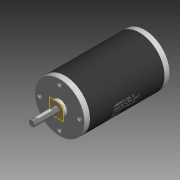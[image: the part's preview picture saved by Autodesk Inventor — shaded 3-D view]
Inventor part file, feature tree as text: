
AUTODESK INVENTOR PART (.ipt)
format: ipt  version: 2018 (Build 220112000, 112)  size: 7,095,296 bytes
history: native  units: mm (DEFAULTED — no unit token found)
features: sketch x10, extrude x7, chamfer x4, plane x3, hole x2, pattern_circular x2, fillet x2, emboss x1, split x1
ambient origin geometry x8: Origin, YZ Plane, XZ Plane, XY Plane, X Axis, Y Axis, Z Axis, Center Point
bodies: Solid1 (feature_tree), Solid2 (feature_tree), Solid3 (feature_tree)
feature tree (32):
  extrude  "Extrusion1"  Depth=7.0mm TaperAngle=0.0deg
  extrude  "Extrusion2"  Depth=3.9878mm TaperAngle=0.0deg
  chamfer  "Chamfer1"  Distance=1.0mm
  hole  "Hole2"  [1 undecoded]
  pattern_circular  "Circular Pattern2"  Count=4 Angle=90.0deg
  chamfer  "Chamfer3"  Distance=31.623mm
  extrude  "Extrusion3"  Depth=12.7mm
  fillet  "Fillet1"  Radius=64.4144mm
  extrude  "Extrusion5"  Depth=64.008mm
  extrude  "Extrusion6"  Depth=7.0mm
  extrude  "Extrusion7"  Depth=0.508mm
  hole  "Hole3"  [1 undecoded]
  chamfer  "Chamfer2"  Distance=20.0mm Angle=360.0deg
  pattern_circular  "Circular Pattern3"  [2 undecoded]
  fillet  "Fillet2"  [1 undecoded]
  chamfer  "Chamfer4"  Distance=1.99898mm
  plane  "Work Plane1"
  extrude  "Extrusion8"  Depth=1.99898mm
  plane  "Work Plane2"
  emboss  "Emboss1"
  plane  "Work Plane3"
  split  "Split1"
  sketch  "Sketch1"  dims[d0=64.008mm d1=7.0mm d2=0.0mm]
  sketch  "Sketch2"  dims[d3=19.05mm d4=3.9878mm d5=0.0mm d6=1.0mm d7=1.0mm]
  sketch  "Sketch4"  dims[d18=3.9624mm d19=9.525mm d20=6.35mm d21=60.0deg d22=19.05mm d23=20.594885mm d24=25.4mm d25=40.0mm d27=90.0deg]
  sketch  "Sketch5"  dims[d28=7.9502mm d29=31.623mm d30=0.0mm]
  sketch  "Sketch8"  dims[d31=0.79375mm d33=12.7mm d38=64.4144mm]
  sketch  "Sketch9"  dims[d39=95.6056mm d40=0.0mm d41=64.008mm]
  sketch  "Sketch10"  dims[d42=7.0mm d43=0.0mm d44=30.1498mm]
  sketch  "Sketch11"  dims[d45=4.1148mm d46=0.0mm]
  sketch  "Sketch12"  dims[d47=5.08mm d48=12.7mm d49=9.906mm d50=4.572mm d51=14.3117mm d52=7.62mm d53=20.594885mm d54=0.508mm d55=3.175mm]
  sketch  "Sketch13"  dims[d56=0.762mm d57=0.762mm d58=3.175mm d59=20.0mm d61=360.0deg d62=0.25mm d63=3.175mm d64=45.0deg d65=45.0deg d66=45.0deg d67=45.0deg d68=1.99898mm d70=20.09902mm d71=7.99338mm d72=1.15062mm d73=0.0mm d74=30.48mm d75=0.0254mm d76=0.0mm d77=0.0mm]
note: 5 required parameter values undecoded (feature->parameter linkage not recoverable at this tier; creation-order binding heuristic only, values carry confidence <= 0.55)
